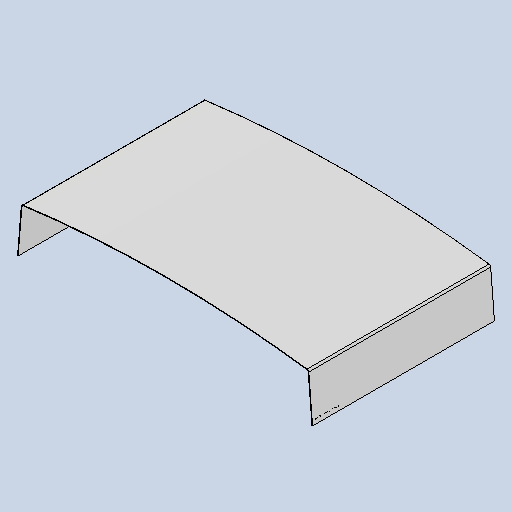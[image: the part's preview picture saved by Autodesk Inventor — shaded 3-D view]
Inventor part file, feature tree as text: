
AUTODESK INVENTOR PART (.ipt)
format: ipt  version: 2025 (Build 290162010, 162A)  size: 300,032 bytes
history: native  units: mm
features: other x4, sheet_metal_op x3, sketch x2, mirror x1
ambient origin geometry x8: Origin, YZ Plane, XZ Plane, XY Plane, X Axis, Y Axis, Z Axis, Center Point
bodies: Body1 (feature_tree)
feature tree (10):
  sheet_metal_op  "Contour Flange2"
  mirror  "Mirror2"
  other  "Mark1"
  other  "A-Side Definition"
  sketch  "Sketch1"  dims[d36=3.0mm]
  other  "Plate2"
  sheet_metal_op  "Bend2"
  sheet_metal_op  "Corner2"
  sketch  "Sketch2"  dims[d37=3.0mm d38=1.5mm d39=6.0mm d40=5.0mm d41=950.0mm d42=5.0mm d43=3.0mm d44=12.0mm d45=3.0mm d46=5.0mm d54=1500.0mm d55=2700.0mm d58=2100.0mm d65=8.0mm d66=8.0mm d78=3.0mm d80=3.0mm d83=8.0mm d113=50.0mm d114=50.0mm d115=3.0mm d121=10.0mm d122=241.9mm d124=16.546129mm]
  other  "Definition1"
